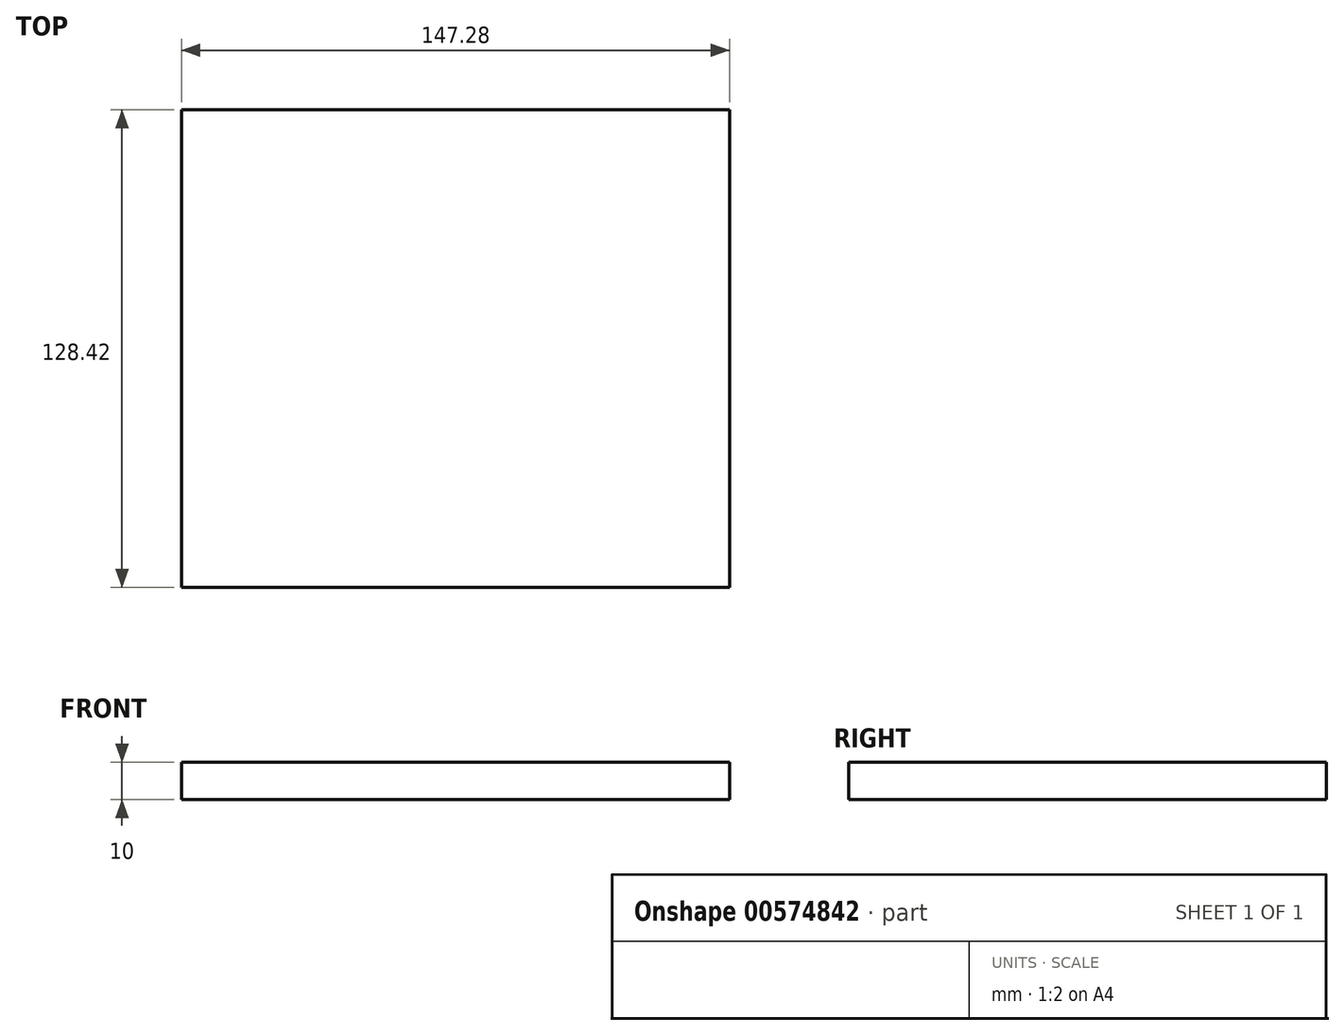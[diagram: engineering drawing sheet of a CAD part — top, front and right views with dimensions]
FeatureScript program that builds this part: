
annotation { "Feature Type Name" : "Feature", "Feature Type Description" : "" }
export const myFeature = defineFeature(function(context is Context, id is Id, definition is map)
    precondition{}
    {
        {
            var Q0;
            Q0=qCreatedBy(makeId("Top.planeOp"),FACE);
            var sketch = newSketch(context, id + "F0", { "sketchPlane" : qUnion([Q0])});
            skLineSegment(sketch, "E0.bottom", {"start": v(105.34, 80.6) * mm, "end": v(-41.94, 80.6) * mm});
            skLineSegment(sketch, "E0.top", {"start": v(105.34, -47.83) * mm, "end": v(-41.94, -47.83) * mm});
            skLineSegment(sketch, "E0.left", {"start": v(105.34, 80.6) * mm, "end": v(105.34, -47.83) * mm});
            skLineSegment(sketch, "E0.right", {"start": v(-41.94, 80.6) * mm, "end": v(-41.94, -47.83) * mm});
            skSolve(sketch);
        }
        {
            var Q0;
            Q0 = qSketchRegion(id + "F0", true);
            extrude(context, id + "F1", {"entities" : qUnion([Q0]), "depth" : 10 * mm, "offsetDistance" : 25 * mm});
        }
    });
